# Revit family: SPADA-LED-xxx-840-MPS
name_source: partatom
category: Leuchten
revit_build: Autodesk Revit 2017 (Build: 20190508_0315(x64)
units: mm (PartAtom-declared; Revit-internal decimal feet)

## family parameters
Basisbauteil = Fläche
Beim Laden mit Abzugskörper schneiden = Nein
Bemaßung runder Anschluss = Durchmesser verwenden
Gemeinsam genutzt = Nein
Lichtquelle = Ja
OmniClass-Nummer = 23.80.70.11
OmniClass-Titel = Luminaries for Internal Lighting
Raumberechnungspunkt = Nein
Teiletyp = Normal

## types (2) — shared parameters
Baugruppenkennzeichen = D5020200
Emissionsform beim Rendern sichtbar = Nein
Farbfilter = 16777215
Farbtemperaturverschiebung bei Dämpfen der Lampe = <Keine Auswahl>
Hersteller = RIDI Leuchten GmbH
Lampe = LED
Neigungswinkel = -90.00°
URL = www.ridi.de
Von Breite des Rechtecks ausssenden = 550 mm
Von Länge des Rechtecks aussenden = 250 mm  [stored 0.82021 ft]
brand = RIDI
conformity mark = CE
electrical safety class = 1
height = 1950 mm  [stored 6.39764 ft]
ingress protection (IP) code = IP20
length = 680 mm  [stored 2.23097 ft]
nominal frequency = 50-60Hz
nominal voltage = 230
voltage type (AC, DC, UC) = AC
weight = 16.4 kg
width = 300 mm
zero-valued in all types: Vorgabe-Ansicht

## per-type parameters (varying)
| type | Datei für fotometrisches Netz | Modell | Scheinlast | rated input power |
| SPADA-LED 7800-840 MPS | SPADA-LED 7800840 MPS.IES | 0627232 | 48 VA | 48 |
| SPADA-LED 13000-840 MPS | SPADA-LED 13000-840 MPS.IES | 0627498 | 86 VA | 86 |

note: column(s) folded — value = type name in every type: product name

note: [stored X ft] marks values corroborated as IEEE doubles in the binary element streams (Revit-internal decimal feet)
